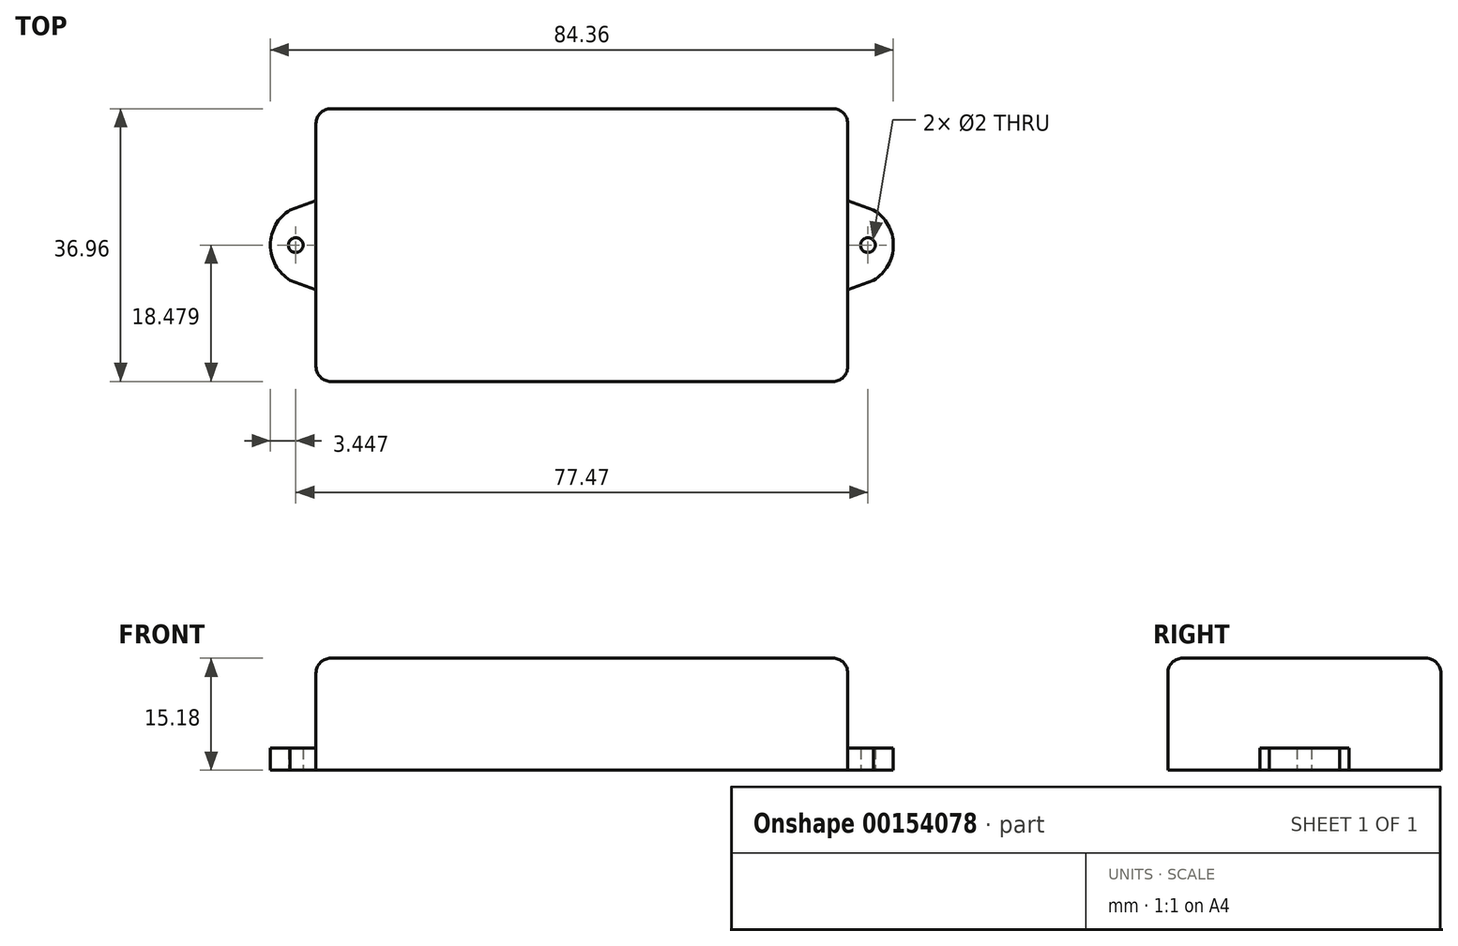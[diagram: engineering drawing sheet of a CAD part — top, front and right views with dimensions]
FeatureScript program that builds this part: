
annotation { "Feature Type Name" : "Feature", "Feature Type Description" : "" }
export const myFeature = defineFeature(function(context is Context, id is Id, definition is map)
    precondition{}
    {
        {
            var Q0;
            Q0=qCreatedBy(makeId("Top.planeOp"),FACE);
            var sketch = newSketch(context, id + "F0", { "sketchPlane" : qUnion([Q0])});
            skLineSegment(sketch, "E0.bottom", {"start": v(0, 0) * mm, "end": v(71.98, 0) * mm});
            skLineSegment(sketch, "E0.top", {"start": v(0, 36.96) * mm, "end": v(71.98, 36.96) * mm});
            skLineSegment(sketch, "E0.left", {"start": v(0, 0) * mm, "end": v(0, 36.96) * mm});
            skLineSegment(sketch, "E0.right", {"start": v(71.98, 0) * mm, "end": v(71.98, 36.96) * mm});
            skLineSegment(sketch, "E1", {"start": v(-29, 18.48) * mm, "end": v(103.73, 18.48) * mm, "construction": true});
            skPoint(sketch, "E1.startSnap0", {"position": v(0, 18.48) * mm});
            skPoint(sketch, "E1.endSnap0", {"position": v(71.98, 18.48) * mm});
            skLineSegment(sketch, "E2", {"start": v(36, 0) * mm, "end": v(36, 57.72) * mm, "construction": true});
            skPoint(sketch, "E3", {"position": v(78.17, 18.48) * mm});
            skPoint(sketch, "E4", {"position": v(-6.18, 18.48) * mm});
            skLineSegment(sketch, "E5", {"start": v(71.98, 24.51) * mm, "end": v(75.48, 23.24) * mm});
            skLineSegment(sketch, "E6", {"start": v(75.48, 13.72) * mm, "end": v(71.98, 12.45) * mm});
            skArc(sketch, "E7", {"start": v(75.48, 13.72) * mm, "mid": v(78.17, 18.48) * mm, "end": v(75.48, 23.24) * mm});
            skCircle(sketch, "E8", {"center": v(74.73, 18.48) * mm, "radius": 1 * mm});
            skLineSegment(sketch, "E9.MirrorCS", {"start": v(0, 24.51) * mm, "end": v(-3.5, 23.24) * mm});
            skArc(sketch, "E10.MirrorCS", {"start": v(-3.5, 13.72) * mm, "mid": v(-6.19, 18.48) * mm, "end": v(-3.5, 23.24) * mm});
            skLineSegment(sketch, "E11.MirrorCS", {"start": v(-3.5, 13.72) * mm, "end": v(0, 12.45) * mm});
            skCircle(sketch, "E12.MirrorC", {"center": v(-2.74, 18.48) * mm, "radius": 1 * mm});
            skSolve(sketch);
        }
        {
            var Q0;
            {var subQ3=sQuery(id+"F0.wireOp",EDGE,"E0.bottom");Q0=makeQuery(id+"F0.imprint","IMPRINT",FACE,{"disambiguationData":[TD([[makeQuery(id+"F0.imprint","IMPRINT",EDGE,{"derivedFrom":subQ3}),1.0]])]});}
            extrude(context, id + "F1", {"entities" : qUnion([Q0]), "depth" : (.854 * 25.4 * .7) * mm});
        }
        {
            var Q0;
            {var subQ1=sQuery(id+"F0.wireOp",EDGE,"E5");Q0=makeQuery(id+"F0.imprint","IMPRINT",FACE,{"disambiguationData":[TD([[makeQuery(id+"F0.imprint","IMPRINT",EDGE,{"derivedFrom":subQ1}),-1.0]])]});}
            var Q1;
            {var subQ1=sQuery(id+"F0.wireOp",EDGE,"E9.MirrorCS");Q1=makeQuery(id+"F0.imprint","IMPRINT",FACE,{"disambiguationData":[TD([[makeQuery(id+"F0.imprint","IMPRINT",EDGE,{"derivedFrom":subQ1}),1.0]])]});}
            extrude(context, id + "F2", {"entities" : qUnion([Q0, Q1]), "operationType" : NewBodyOperationType.ADD, "depth" : 3 * mm});
        }
        {
            var Q0;
            Q0=makeQuery(id+"F1.opExtrude","CAP_FACE",FACE,{"disambiguationData":[OSD([sQuery(id+"F0.wireOp",EDGE,"E0.bottom"),sQuery(id+"F0.wireOp",EDGE,"E0.top"),sQuery(id+"F0.wireOp",EDGE,"E0.left"),sQuery(id+"F0.wireOp",EDGE,"E0.right")])],"isStart":false});
            var Q1;
            Q1=makeQuery(id+"F1.opExtrude","SWEPT_EDGE",EDGE,{"disambiguationData":[OSD([sQuery(id+"F0.wireOp",EDGE,"E0.top"),sQuery(id+"F0.wireOp",EDGE,"E0.left")])]});
            var Q2;
            Q2=makeQuery(id+"F1.opExtrude","SWEPT_EDGE",EDGE,{"disambiguationData":[OSD([sQuery(id+"F0.wireOp",EDGE,"E0.top"),sQuery(id+"F0.wireOp",EDGE,"E0.right")])]});
            var Q3;
            Q3=makeQuery(id+"F1.opExtrude","SWEPT_EDGE",EDGE,{"disambiguationData":[OSD([sQuery(id+"F0.wireOp",EDGE,"E0.bottom"),sQuery(id+"F0.wireOp",EDGE,"E0.right")])]});
            var Q4;
            Q4=makeQuery(id+"F1.opExtrude","SWEPT_EDGE",EDGE,{"disambiguationData":[OSD([sQuery(id+"F0.wireOp",EDGE,"E0.bottom"),sQuery(id+"F0.wireOp",EDGE,"E0.left")])]});
            fillet(context, id + "F3", {"entities" : qUnion([Q0, Q1, Q2, Q3, Q4]), "radius" : 2 * mm, "tangentPropagation" : true, "allowEdgeOverflow" : false});
        }
    });
